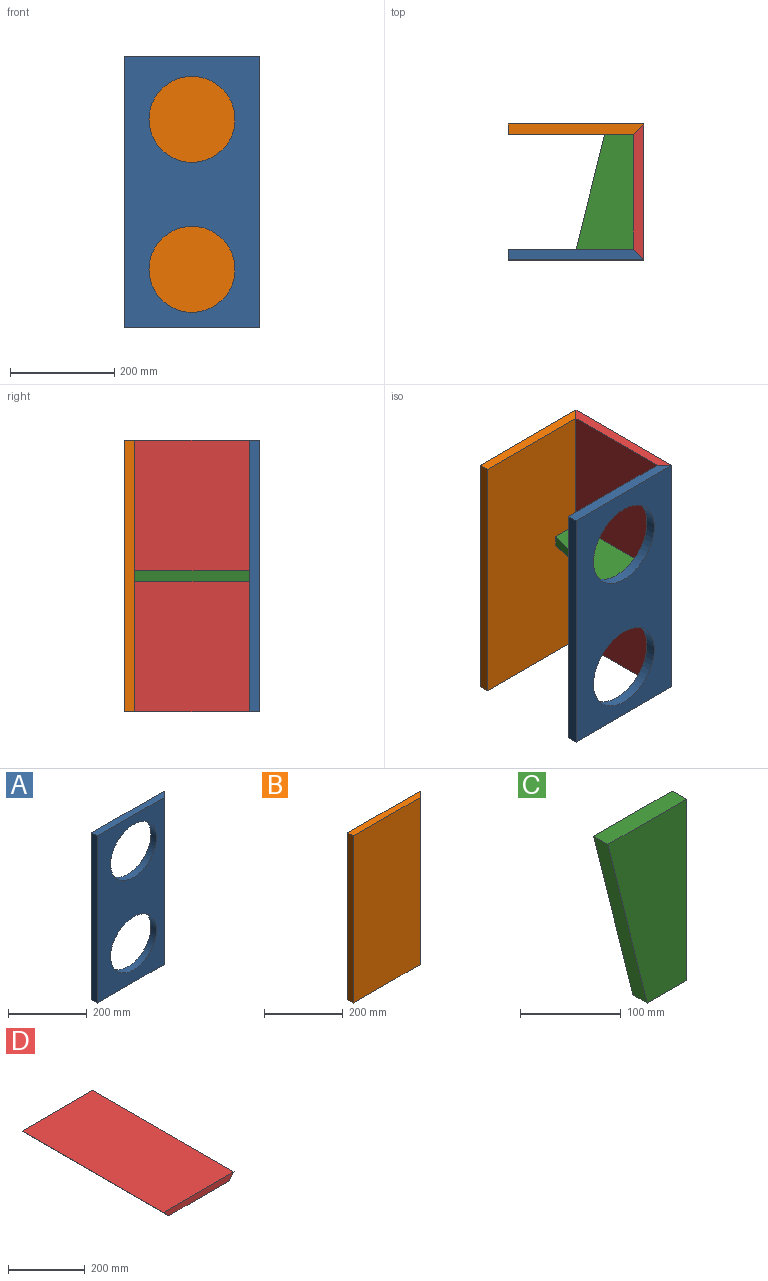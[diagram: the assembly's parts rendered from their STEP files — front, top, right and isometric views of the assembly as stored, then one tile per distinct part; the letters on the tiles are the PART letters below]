
ASSEMBLY  parts=4 mates=3
PART A: 8 faces, bbox 260x20x520 mm
  f0: plane 520x20mm, normal (-1,0,0), area 10400mm2, adj f1,f3,f4,f5
  f1: plane 520x240mm, normal (0,-1,0), area 82035.1mm2, adj f0,f2,f4,f5,f6,f7
  f2: plane 520x20mm, normal (0.71,-0.71,0), area 14707.8mm2, adj f1,f3,f4,f5
  f3: plane 520x260mm, normal (0,1,0), area 92435.1mm2, adj f0,f2,f4,f5,f6,f7
  f4: plane 260x20mm, normal (0,0,1), area 5000mm2, adj f0,f1,f2,f3
  f5: plane 260x20mm, normal (0,0,-1), area 5000mm2, adj f0,f1,f2,f3
  f6: cylinder r=82.5mm len=165mm, axis (0,1,0), area 10367.3mm2, adj f1,f3
  f7: cylinder r=82.5mm len=165mm, axis (0,1,0), area 10367.3mm2, adj f1,f3
PART B: 6 faces, bbox 260x20x520 mm
  f0: plane 520x20mm, normal (-1,0,0), area 10400mm2, adj f1,f3,f4,f5
  f1: plane 520x240mm, normal (0,-1,0), area 124800mm2, adj f0,f2,f4,f5
  f2: plane 520x20mm, normal (0.71,-0.71,0), area 14707.8mm2, adj f1,f3,f4,f5
  f3: plane 520x260mm, normal (0,1,0), area 135200mm2, adj f0,f2,f4,f5
  f4: plane 260x20mm, normal (0,0,1), area 5000mm2, adj f0,f1,f2,f3
  f5: plane 260x20mm, normal (0,0,-1), area 5000mm2, adj f0,f1,f2,f3
PART C: 6 faces, bbox 110x20x220 mm
  f0: plane 55x20mm, normal (0,0,-1), area 1100mm2, adj f1,f3,f4,f5
  f1: plane 220x20mm, normal (1,0,0), area 4400mm2, adj f0,f2,f4,f5
  f2: plane 110x20mm, normal (0,0,1), area 2200mm2, adj f1,f3,f4,f5
  f3: plane 220x55mm, normal (-0.97,0,-0.24), area 4535.4mm2, adj f0,f2,f4,f5
  f4: plane 220x110mm, normal (0,-1,0), area 18150mm2, adj f0,f1,f2,f3
  f5: plane 220x110mm, normal (0,1,0), area 18150mm2, adj f0,f1,f2,f3
PART D: 6 faces, bbox 260x520x20 mm
  f0: plane 520x20mm, normal (-0.71,0,-0.71), area 14707.8mm2, adj f1,f3,f4,f5
  f1: plane 520x220mm, normal (0,0,-1), area 114400mm2, adj f0,f2,f4,f5
  f2: plane 520x20mm, normal (0.71,0,-0.71), area 14707.8mm2, adj f1,f3,f4,f5
  f3: plane 520x260mm, normal (0,0,1), area 135200mm2, adj f0,f2,f4,f5
  f4: plane 260x20mm, normal (0,-1,0), area 4800mm2, adj f0,f1,f2,f3
  f5: plane 260x20mm, normal (0,1,0), area 4800mm2, adj f0,f1,f2,f3
PLACE A rot(axis=(-1,0,0),180deg) t=(-589.52,34.32,424.36)mm
PLACE B rot(axis=(-0.1,-0.01,-1),0deg) t=(-589.52,254.32,-95.64)mm
PLACE C rot(axis=(1,0,0),90deg) t=(-349.52,254.32,174.36)mm
PLACE D rot(axis=(-0.58,0.58,-0.58),120deg) t=(-349.52,254.32,-95.64)mm
MATE fastened A.f2 <-> D.f2  axis (0.71,0.71,0) through (-339.52,24.32,164.36)mm
MATE fastened D.f1 <-> C.f1  axis (-1,0,0) through (-349.52,144.32,164.36)mm
MATE fastened D.f0 <-> B.f2  axis (-0.71,0.71,0) through (-339.52,264.32,164.36)mm
